# Revit family: PRD_AR_WshbsnTps_F5S-MixSelf-closingSingle-mixer_F5SM1011 2
name_source: partatom
category: Plumbing Fixtures
units: mm (PartAtom-declared; Revit-internal decimal feet)

## family parameters
Cut with Voids When Loaded = No
Enable Cutting in Views = No
Host = Face
Maintain Annotation Orientation = No
OmniClass Number = 23.45.55.14
OmniClass Title = Single Faucets
Part Type = Normal
Room Calculation Point = No
Round Connector Dimension = Use Diameter
Shared = No

## types (1)
- F5SM1011
    AccentColour = none
    AdjustableFlowTime = yes
    AssetType = Fixed
    BIMObjectName = PRD_AR_WashbasinTaps_F5S-MixSelf-closingSingle-mixer_F5SM1011
    BasicColour = chrome-look (glossy)
    CalculationFlowRateColdWater = 0.07 l/s
    CalculationFlowRateHotWater = 0.07 l/s
    Category = Pr_40_20_87_98, Washbasin taps
    Default Elevation = 1050 mm
    Depressurised = no
    Description = F5S-Mix Self-closing single-mixer DN 15 with angled outlet for installation on fitting units or separate wall flanges, for sanitary facilities. FRAMIC self-closing mixing cartridge, hydraulically controlled, low-maintenance and stagnation-free, with ceramic disc technology, automatic closing, flow pressure independent due to medium-independent design. Continuously adjustable flow duration. With adjustable, turn-proof temperature stop. For connection to hot and cold water. All-metal construction, high-polished chrome-plated brass. Anti-theft aerator, SLIM design, with integrated flow regulator 5.0 l/min. Connections positioned above one another with backflow preventers.
    DiameterNominal = DN 15
    Export Type to IFC As = IfcValveType
    FaucetFunction = MIXED
    FaucetOperation = SELFCLOSING
    FaucetType = SINGLEOUTLETCOMBINATION
    Features = For connection to hot and cold water. High-polished chrome-plated brass. With integrated flow regulator 5.0 l/min.
    Finish = high-polished chromium-plated brass
    FlowColdWater = 0.1 L/s
    FlowHotWater = 0.1 L/s
    FunctionalPrinciple = hydraulic self-closing
    HygieneFlushing = no
    IfcExportAs = IfcValveType
    IfcExportType = FAUCET
    Inlet = 15  [stored 0.0492126 ft]
    InletSize = DN 15
    LockingMechanism = Top section, non-ceramic
    Manufacturer = KWC Group Management AG
    ManufacturerName = KWC Group Management AG
    ManufacturerURL = www.kwc-professional.com
    Material = chrome-plated brass
    MaterialFitting = brass-look
    MaximumFlowTime = 35 Seconds
    MinimumFlowPressure = 0.5 bar
    MinimumFlowTime = 5 Seconds
    Model = F5SM1011
    ModelNumber = 2030058991
    ModelReference = F5SM1011
    NBSDescription = Water supply fittings for wash basins and troughs
    NBSReference = 45-35-70/371
    Name = F5S-Mix Self-closing single-mixer for fitting unit or wall flange F5SM1011
    NominalDepth = 175 mm  [stored 0.574147 ft]
    NominalHeight = 0 mm  [stored 0 ft]
    NominalLength = 175 mm  [stored 0.574147 ft]
    NominalWidth = 50 mm  [stored 0.164042 ft]
    OutletMaterial = PRD_AR_SyntheticGrey
    Pop-UpWasteSet = no
    ProductInformation = http://pim.kwc.com
    ProtectiveShutdown = no
    Spout = fixed
    SpoutProjection = 110 mm
    SurfaceFinishFitting = chromed
    SurfaceTreatmentFitting = polished
    TailorMade = no
    TapMaterial = PRD_AR_ChromatedBrass_HighPolished
    TemperatureLimit = yes
    ThermalDisinfection = no
    Type IFC Predefined Type = FAUCET
    TypeOfMixing = yes
    TypeOfMounting = mounted on product
    TypeOfOperation = manual operation
    TypeOfTap = for fitting unit
    URL = www.kwc-professional.com
    Uniclass2015Code = Pr_40_20_87_98
    Uniclass2015Title = Washbasin taps
    Uniclass2015Version = Products v1.38
    Version = 1
    VolumeFlowRateAt3Bar = 0.08 l/s
    WaterConnection = plug connection
    WithBackflowPreventer = yes
    WithFilter = yes
    WithRosettes/CoverPlate = no

note: [stored X ft] marks values corroborated as IEEE doubles in the binary element streams (Revit-internal decimal feet)

## geometry (parser evidence)
native form markers: Sweep x4
no freeform markers — native parametric forms only
